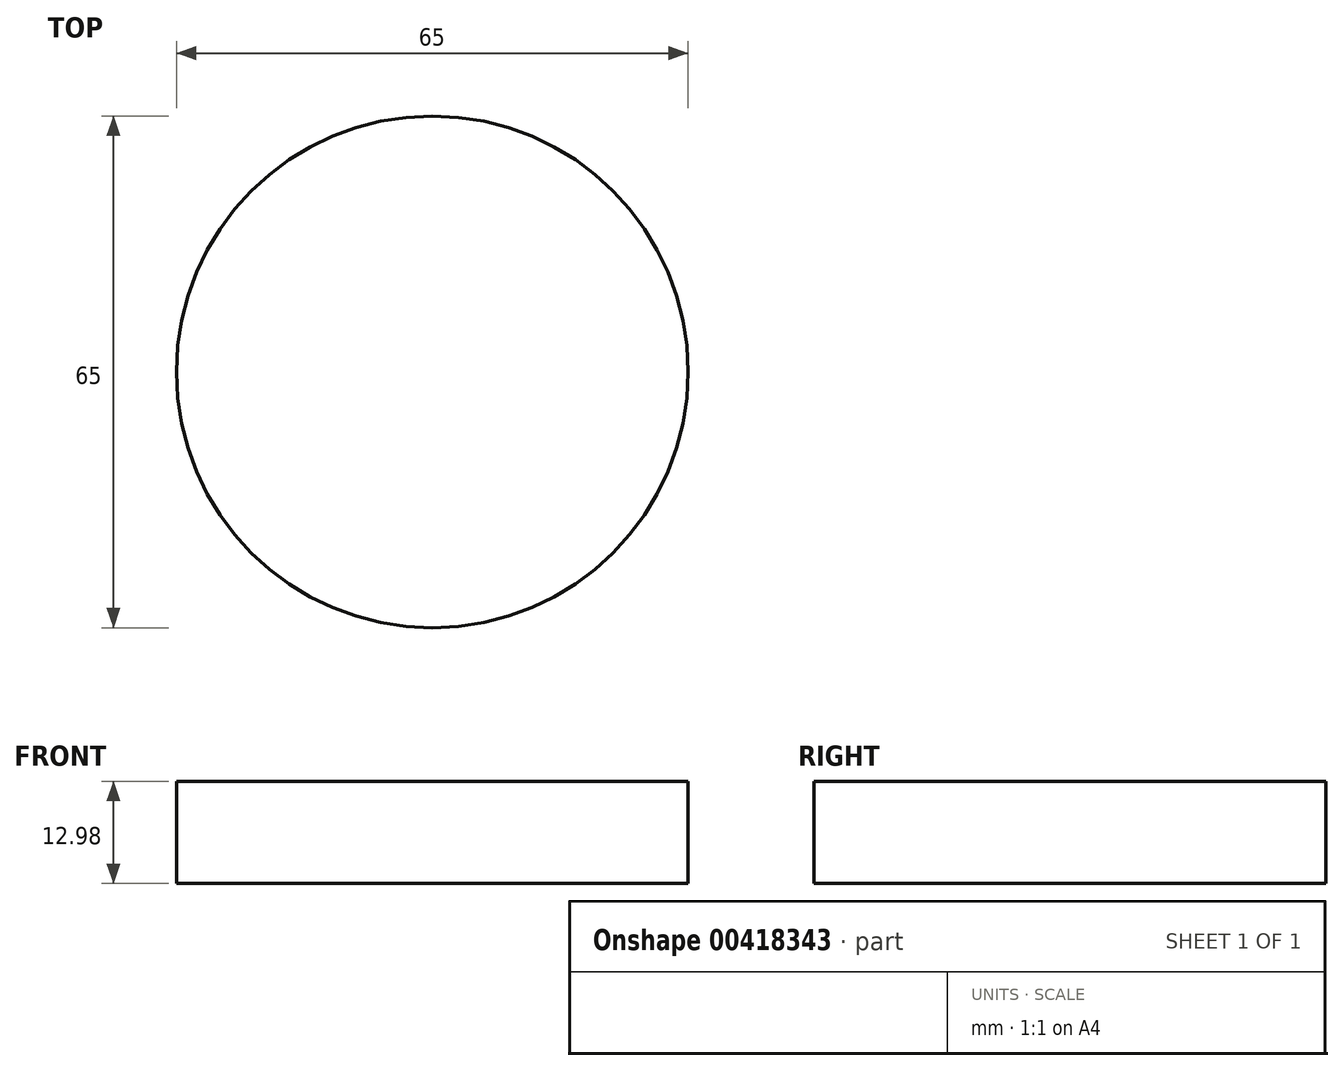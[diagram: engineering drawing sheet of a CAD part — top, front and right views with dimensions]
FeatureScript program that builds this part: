
annotation { "Feature Type Name" : "Feature", "Feature Type Description" : "" }
export const myFeature = defineFeature(function(context is Context, id is Id, definition is map)
    precondition{}
    {
        {
            var Q0;
            Q0=qCreatedBy(makeId("Top.planeOp"),FACE);
            var sketch = newSketch(context, id + "F0", { "sketchPlane" : qUnion([Q0])});
            skCircle(sketch, "E0", {"center": v(-32, 27.11) * mm, "radius": 32.5 * mm});
            skSolve(sketch);
        }
        {
            var Q0;
            Q0 = qSketchRegion(id + "F0", true);
            extrude(context, id + "F1", {"entities" : qUnion([Q0]), "depth" : 12.98 * mm});
        }
    });
